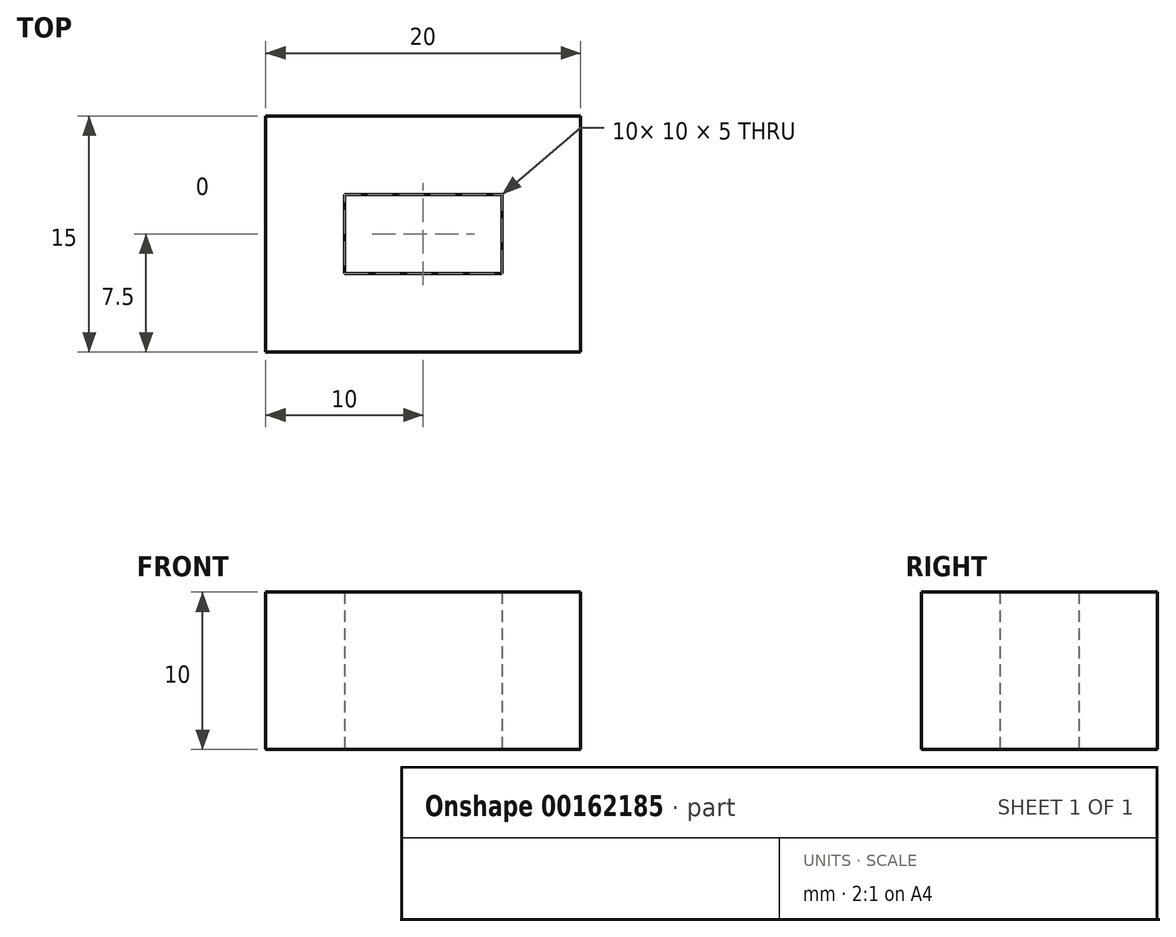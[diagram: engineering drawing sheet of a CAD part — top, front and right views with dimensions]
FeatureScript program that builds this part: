
annotation { "Feature Type Name" : "Feature", "Feature Type Description" : "" }
export const myFeature = defineFeature(function(context is Context, id is Id, definition is map)
    precondition{}
    {
        {
            var Q0;
            Q0=qCreatedBy(makeId("Top.planeOp"),FACE);
            var sketch = newSketch(context, id + "F0", { "sketchPlane" : qUnion([Q0])});
            skLineSegment(sketch, "E0.bottom", {"start": v(-5, 2.5) * mm, "end": v(5, 2.5) * mm});
            skLineSegment(sketch, "E0.top", {"start": v(-5, -2.5) * mm, "end": v(5, -2.5) * mm});
            skLineSegment(sketch, "E0.left", {"start": v(-5, 2.5) * mm, "end": v(-5, -2.5) * mm});
            skLineSegment(sketch, "E0.right", {"start": v(5, 2.5) * mm, "end": v(5, -2.5) * mm});
            skPoint(sketch, "E0.middle", {"position": v(0, 0) * mm});
            skLineSegment(sketch, "E1.bottom", {"start": v(-10, 7.5) * mm, "end": v(10, 7.5) * mm});
            skLineSegment(sketch, "E1.top", {"start": v(-10, -7.5) * mm, "end": v(10, -7.5) * mm});
            skLineSegment(sketch, "E1.left", {"start": v(-10, 7.5) * mm, "end": v(-10, -7.5) * mm});
            skLineSegment(sketch, "E1.right", {"start": v(10, 7.5) * mm, "end": v(10, -7.5) * mm});
            skSolve(sketch);
        }
        {
            var Q0;
            Q0=makeQuery(id+"F0.imprint","IMPRINT",FACE,{"disambiguationData":[TD([[makeQuery(id+"F0.imprint","IMPRINT",EDGE,{"derivedFrom":sQuery(id+"F0.wireOp",EDGE,"E0.bottom")}),1.0]])]});
            extrude(context, id + "F1", {"entities" : qUnion([Q0]), "depth" : 10 * mm});
        }
    });
